# Revit family: Faucet-Lavatory-KOHLER-Honesty-K-99760-4
name_source: partatom
category: Plumbing Fixtures
revit_build: Autodesk Revit 2015 (Build: 20140606_1530(x64)
units: mm (PartAtom-declared; Revit-internal decimal feet)

## types (1)
- CP-Polished Chrome
    ADA Compliant = Yes
    Assembly Code = D2020300
    CW Connection = Yes
    Date Modified = 09/17/2017
    Default Elevation = 42"
    Description = Honesty®single-handle bathroom sink faucet
    Finish = Metal - Kohler- CP- Polished Chrome
    Flow Rate = 1 GPM
    HW Connection = Yes
    Height = 4 3/4"
    Inlet Connection = Inlet Connection
    Length = 5 11/16"
    Manufacturer = Kohler
    MasterFormat 1995 = 15410
    MasterFormat 2004 = 22.41.39
    Material = Brass Construction
    Model = K-99760-4-CP
    Outlet Connection = Outlet Connection
    Product Documentation Link = http://www.us.kohler.com
    Product Name = Honesty
    Product Page URL = http://www.us.kohler.com
    Spout Reach = 4 3/16"
    URL = http://www.us.kohler.com
    Waste Connection Diameter = 0"
    Width = 1 3/4"

## geometry (parser evidence)
native form markers: Blend x4, Sweep x4
no freeform markers — native parametric forms only
